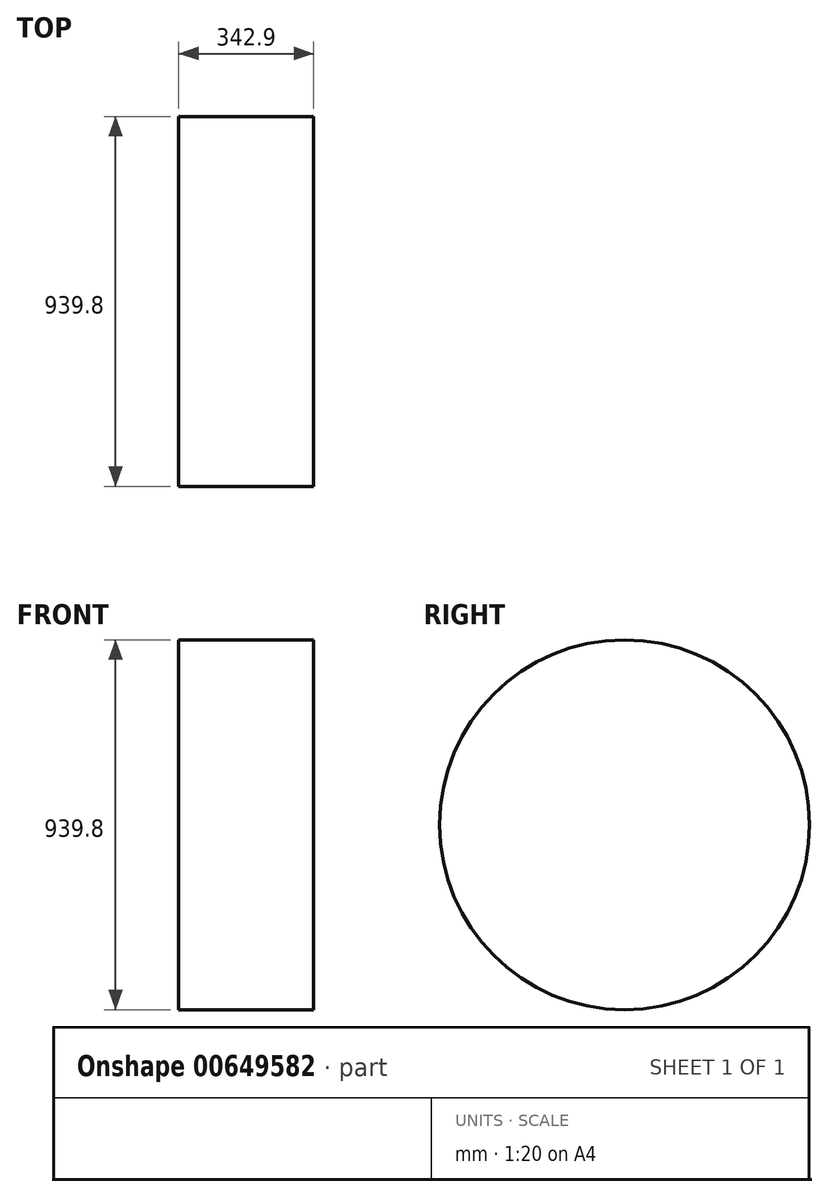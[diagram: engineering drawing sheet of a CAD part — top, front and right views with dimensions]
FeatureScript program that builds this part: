
annotation { "Feature Type Name" : "Feature", "Feature Type Description" : "" }
export const myFeature = defineFeature(function(context is Context, id is Id, definition is map)
    precondition{}
    {
        {
            var Q0;
            Q0=qCreatedBy(makeId("Right.planeOp"), FACE);
            var sketch = newSketch(context, id + "F0", { "sketchPlane" : qUnion([Q0])});
            skCircle(sketch, "E0", {"center": v(0, 0) * mm, "radius": 469.9 * mm});
            skSolve(sketch);
        }
        {
            var Q0;
            Q0 = qSketchRegion(id + "F0", true);
            extrude(context, id + "F1", {"entities" : qUnion([Q0]), "oppositeDirection" : true, "depth" : 342.9 * mm, "offsetDistance" : 25.4 * mm});
        }
    });
